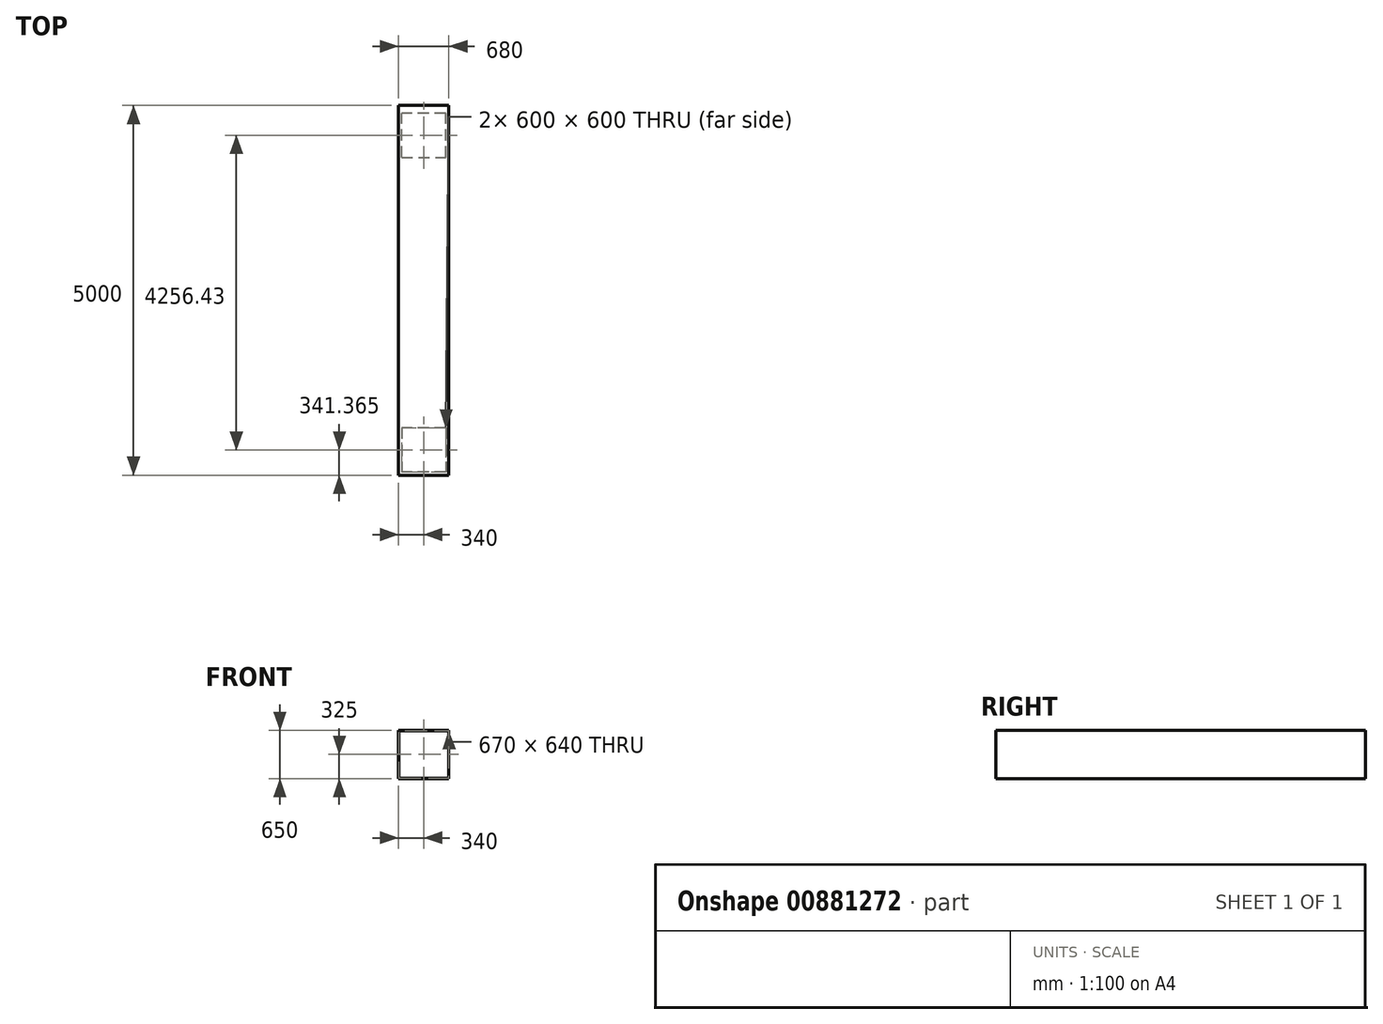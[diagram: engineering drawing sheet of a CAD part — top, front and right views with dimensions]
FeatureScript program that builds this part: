
annotation { "Feature Type Name" : "Feature", "Feature Type Description" : "" }
export const myFeature = defineFeature(function(context is Context, id is Id, definition is map)
    precondition{}
    {
        {
            var Q0;
            Q0=qCreatedBy(makeId("Front.planeOp"),FACE);
            var sketch = newSketch(context, id + "F0", { "sketchPlane" : qUnion([Q0])});
            skLineSegment(sketch, "E0", {"start": v(335, 0) * mm, "end": v(335, 335) * mm});
            skLineSegment(sketch, "E1", {"start": v(335, 335) * mm, "end": v(-335, 335) * mm});
            skLineSegment(sketch, "E2", {"start": v(-335, 335) * mm, "end": v(-335, 0) * mm});
            skLineSegment(sketch, "E3.0", {"start": v(340, 0) * mm, "end": v(340, 340) * mm});
            skLineSegment(sketch, "E3.1", {"start": v(-340, 340) * mm, "end": v(-340, 0) * mm});
            skLineSegment(sketch, "E3.3", {"start": v(340, 340) * mm, "end": v(-340, 340) * mm});
            skLineSegment(sketch, "E4", {"start": v(-335, 0) * mm, "end": v(-335, -305) * mm});
            skLineSegment(sketch, "E5.MirrorCS", {"start": v(335, 0) * mm, "end": v(335, -305) * mm});
            skLineSegment(sketch, "E6", {"start": v(335, -305) * mm, "end": v(-335, -305) * mm});
            skLineSegment(sketch, "E7.0", {"start": v(-340, 0) * mm, "end": v(-340, -310) * mm});
            skLineSegment(sketch, "E7.1", {"start": v(340, -310) * mm, "end": v(-340, -310) * mm});
            skLineSegment(sketch, "E7.2", {"start": v(340, 0) * mm, "end": v(340, -310) * mm});
            skSolve(sketch);
        }
        {
            var Q0;
            Q0 = qSketchRegion(id + "F0", true);
            extrude(context, id + "F1", {"entities" : qUnion([Q0]), "depth" : 5000 * mm, "offsetDistance" : 25 * mm});
        }
        {
            var Q0;
            Q0=makeQuery(id+"F1.opExtrude","SWEPT_FACE",FACE,{"disambiguationData":[OSD([sQuery(id+"F0.wireOp",EDGE,"E7.1")])]});
            var sketch = newSketch(context, id + "F2", { "sketchPlane" : qUnion([Q0])});
            skLineSegment(sketch, "E8", {"start": v(0, 4358.63) * mm, "end": v(300, 4358.63) * mm});
            skLineSegment(sketch, "E9", {"start": v(300, 4358.63) * mm, "end": v(300, 4958.63) * mm});
            skLineSegment(sketch, "E10", {"start": v(300, 4958.63) * mm, "end": v(0, 4958.63) * mm});
            skLineSegment(sketch, "E11.MirrorCS", {"start": v(-300, 4358.63) * mm, "end": v(-300, 4958.63) * mm});
            skLineSegment(sketch, "E12.MirrorCS", {"start": v(0, 4358.63) * mm, "end": v(-300, 4358.63) * mm});
            skLineSegment(sketch, "E13.MirrorCS", {"start": v(-300, 4958.63) * mm, "end": v(0, 4958.63) * mm});
            skLineSegment(sketch, "E14", {"start": v(0, 702.2) * mm, "end": v(-300, 702.2) * mm});
            skLineSegment(sketch, "E15", {"start": v(-300, 702.2) * mm, "end": v(-300, 102.2) * mm});
            skLineSegment(sketch, "E16", {"start": v(0, 702.2) * mm, "end": v(0, 402.2) * mm});
            skLineSegment(sketch, "E17.MirrorCS", {"start": v(300, 702.2) * mm, "end": v(300, 102.2) * mm});
            skLineSegment(sketch, "E18.MirrorCS", {"start": v(0, 702.2) * mm, "end": v(300, 702.2) * mm});
            skLineSegment(sketch, "E19", {"start": v(0, 402.2) * mm, "end": v(167.29, 402.2) * mm});
            skLineSegment(sketch, "E20.MirrorCS", {"start": v(0, 102.2) * mm, "end": v(300, 102.2) * mm});
            skLineSegment(sketch, "E21.MirrorCS", {"start": v(0, 102.2) * mm, "end": v(-300, 102.2) * mm});
            skSolve(sketch);
        }
        {
            var Q0;
            Q0 = qSketchRegion(id + "F2", true);
            extrude(context, id + "F3", {"entities" : qUnion([Q0]), "operationType" : NewBodyOperationType.REMOVE, "oppositeDirection" : true, "depth" : 25 * mm, "offsetDistance" : 25 * mm});
        }
    });
